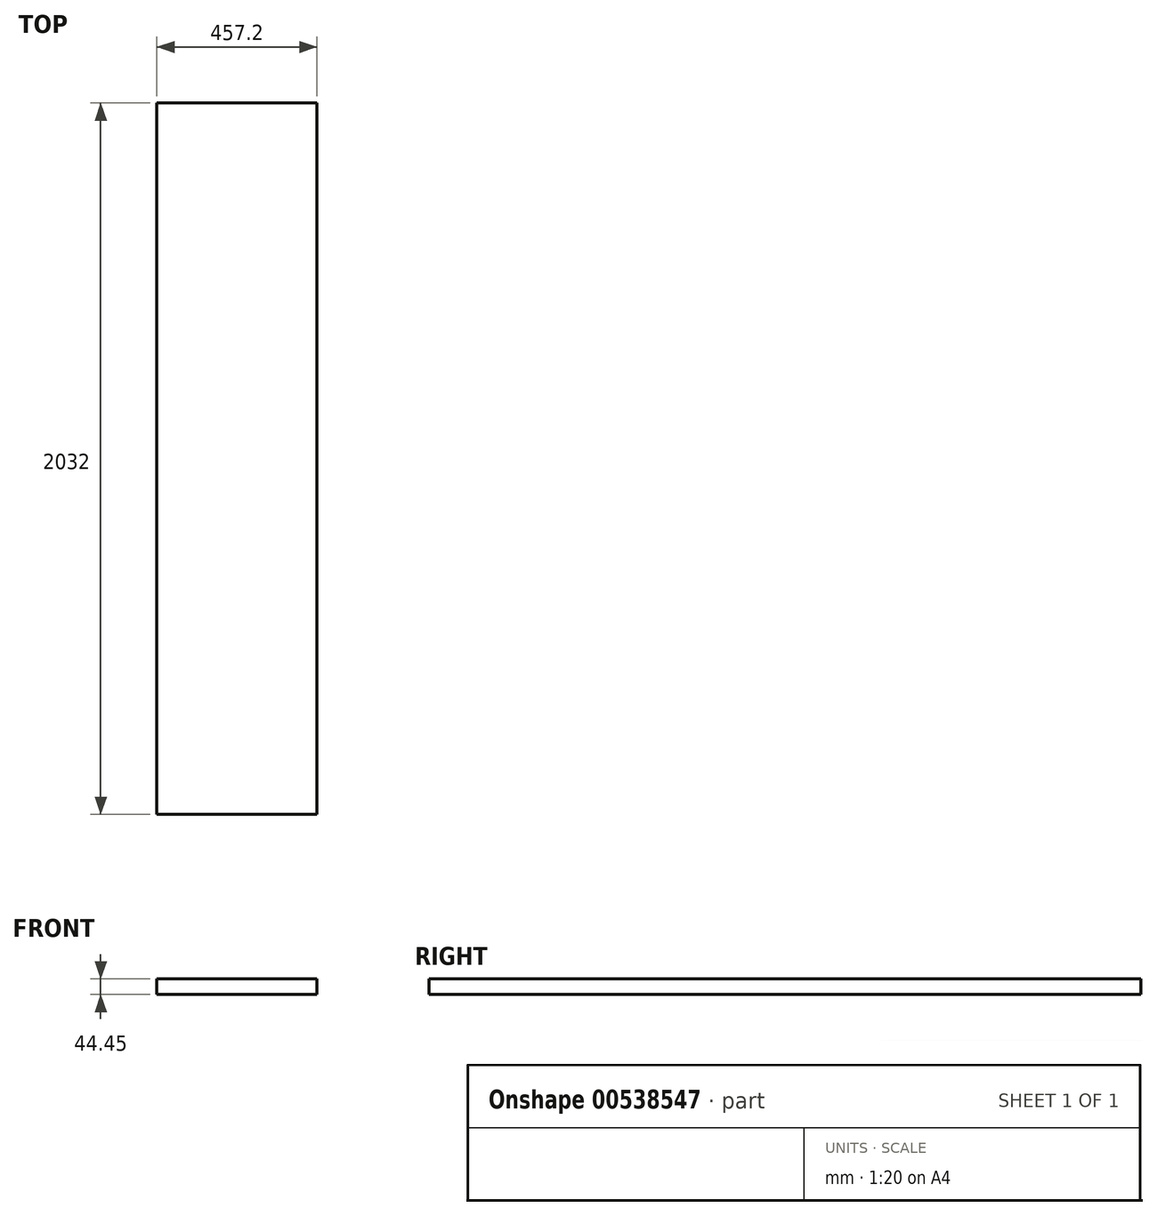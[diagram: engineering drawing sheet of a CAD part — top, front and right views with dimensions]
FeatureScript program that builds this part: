
annotation { "Feature Type Name" : "Feature", "Feature Type Description" : "" }
export const myFeature = defineFeature(function(context is Context, id is Id, definition is map)
    precondition{}
    {
        {
            var Q0;
            Q0=qCreatedBy(makeId("Top.planeOp"),FACE);
            var sketch = newSketch(context, id + "F0", { "sketchPlane" : qUnion([Q0])});
            skLineSegment(sketch, "E0.bottom", {"start": v(-228.6, 1016) * mm, "end": v(228.6, 1016) * mm});
            skLineSegment(sketch, "E0.top", {"start": v(-228.6, -1016) * mm, "end": v(228.6, -1016) * mm});
            skLineSegment(sketch, "E0.left", {"start": v(-228.6, 1016) * mm, "end": v(-228.6, -1016) * mm});
            skLineSegment(sketch, "E0.right", {"start": v(228.6, 1016) * mm, "end": v(228.6, -1016) * mm});
            skPoint(sketch, "E0.middle", {"position": v(0, 0) * mm});
            skSolve(sketch);
        }
        {
            var Q0;
            Q0=makeQuery(id+"F0.imprint","IMPRINT",FACE,{"disambiguationData":[TD([[makeQuery(id+"F0.imprint","IMPRINT",EDGE,{"derivedFrom":sQuery(id+"F0.wireOp",EDGE,"E0.bottom")}),-1.0]])]});
            extrude(context, id + "F1", {"entities" : qUnion([Q0]), "depth" : 44.45 * mm, "offsetDistance" : 25.4 * mm});
        }
    });
